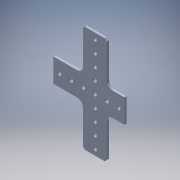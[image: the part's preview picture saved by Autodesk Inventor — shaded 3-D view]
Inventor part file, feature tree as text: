
AUTODESK INVENTOR PART (.ipt)
format: ipt  version: 2017 (Build 210142000, 142)  size: 167,424 bytes
history: native  units: in
note: dims shown in document units (in); Inventor stores cm internally (conversion verified against a paired STEP export)
features: extrude x2, sketch x2, other x1
ambient origin geometry x8: Origin, YZ Plane, XZ Plane, XY Plane, X Axis, Y Axis, Z Axis, Center Point
bodies: Solid1 (feature_tree)
feature tree (5):
  extrude  "Extrusion1"  Depth=0.5in
  extrude  "Extrusion2"  Depth=1.0in
  sketch  "Sketch1"  dims[d0=0.5in d1=1.2in]
  sketch  "Sketch2"  dims[d2=1.0in d3=0.0in d4=1.0in d5=1.0in d6=0.0in]
  other  "Break-Corner1"
